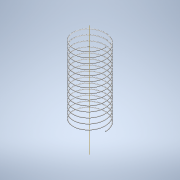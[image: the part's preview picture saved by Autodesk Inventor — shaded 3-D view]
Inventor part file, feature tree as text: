
AUTODESK INVENTOR PART (.ipt)
format: ipt  version: 2020 (Build 240168000, 168)  size: 347,136 bytes
history: native  units: mm
features: helix x1, other x1, sketch x1
ambient origin geometry x8: Origin, YZ Plane, XZ Plane, XY Plane, X Axis, Y Axis, Z Axis, Center Point
bodies: Solid1 (feature_tree)
feature tree (3):
  helix  "Coil1"  [1 undecoded]
  other  "Work Axis1"
  sketch  "Sketch1"  dims[d1=0.3mm d2=10.0mm d3=32.0mm d4=140.0mm d5=0.0mm d6=90.0deg d7=90.0deg d8=0.0mm d9=0.0mm]
note: 1 required parameter value undecoded (feature->parameter linkage not recoverable at this tier; creation-order binding heuristic only, values carry confidence <= 0.55)
